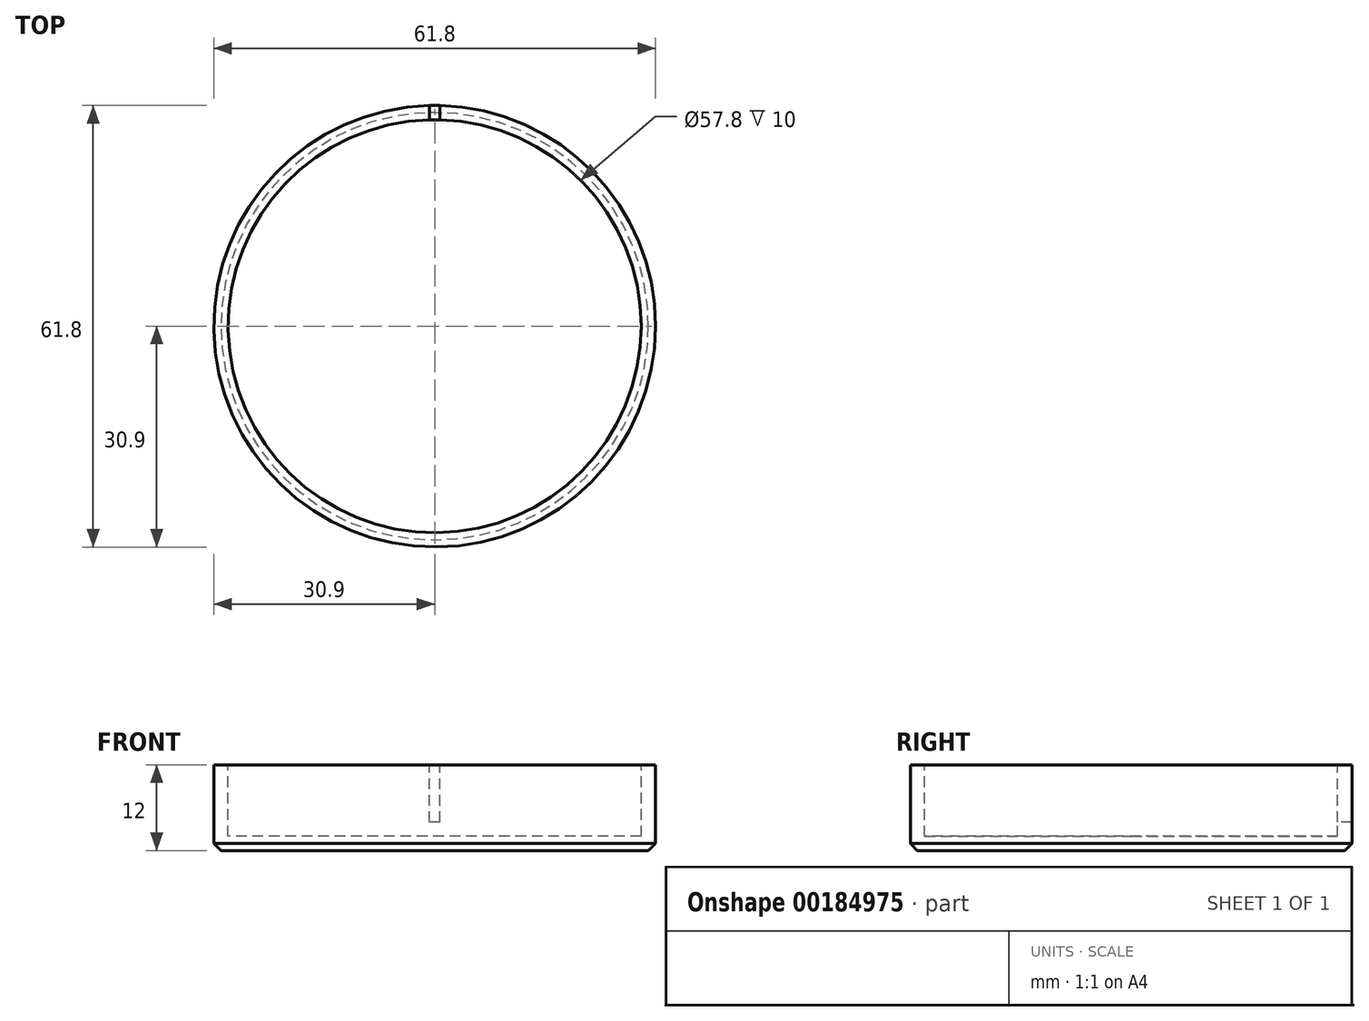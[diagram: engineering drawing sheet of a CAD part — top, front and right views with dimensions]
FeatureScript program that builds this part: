
annotation { "Feature Type Name" : "Feature", "Feature Type Description" : "" }
export const myFeature = defineFeature(function(context is Context, id is Id, definition is map)
    precondition{}
    {
        {
            var Q0;
            Q0=qCreatedBy(makeId("Front.planeOp"),FACE);
            var sketch = newSketch(context, id + "F0", { "sketchPlane" : qUnion([Q0])});
            skLineSegment(sketch, "E0", {"start": v(0, 0) * mm, "end": v(-30.9, 0) * mm});
            skLineSegment(sketch, "E1", {"start": v(-30.9, 0) * mm, "end": v(-30.9, 12) * mm});
            skLineSegment(sketch, "E2", {"start": v(-30.9, 12) * mm, "end": v(-28.9, 12) * mm});
            skLineSegment(sketch, "E3", {"start": v(-28.9, 12) * mm, "end": v(-28.9, 2) * mm});
            skLineSegment(sketch, "E4", {"start": v(-28.9, 2) * mm, "end": v(0, 2) * mm});
            skLineSegment(sketch, "E5", {"start": v(0, 2) * mm, "end": v(0, 0) * mm});
            skSolve(sketch);
        }
        {
            var Q0;
            Q0=makeQuery(id+"F0.imprint","IMPRINT",FACE,{"disambiguationData":[TD([[makeQuery(id+"F0.imprint","IMPRINT",EDGE,{"derivedFrom":sQuery(id+"F0.wireOp",EDGE,"E0")}),-1.0]])]});
            var Q1;
            Q1=sQuery(id+"F0.wireOp",EDGE,"E5");
            revolve(context, id + "F1", {"entities" : qUnion([Q0]), "axis" : qUnion([Q1]), "revolveType" : RevolveType.FULL});
        }
        {
            var Q0;
            Q0=qCreatedBy(makeId("Top.planeOp"),FACE);
            cPlane(context, id + "F2", {"entities" : qUnion([Q0]), "cplaneType" : CPlaneType.OFFSET, "offset" : 12 * mm, "width" : 150 * mm, "height" : 150 * mm});
        }
        {
            var Q0;
            Q0=qCreatedBy(id+"F2.planeOp",FACE);
            var sketch = newSketch(context, id + "F3", { "sketchPlane" : qUnion([Q0])});
            skLineSegment(sketch, "E6.bottom", {"start": v(-0.75, 31.53) * mm, "end": v(0.75, 31.53) * mm});
            skLineSegment(sketch, "E6.top", {"start": v(-0.75, 27.23) * mm, "end": v(0.75, 27.23) * mm});
            skLineSegment(sketch, "E6.left", {"start": v(-0.75, 31.53) * mm, "end": v(-0.75, 27.23) * mm});
            skLineSegment(sketch, "E6.right", {"start": v(0.75, 31.53) * mm, "end": v(0.75, 27.23) * mm});
            skSolve(sketch);
        }
        {
            var Q0;
            Q0=makeQuery(id+"F3.imprint","IMPRINT",FACE,{"disambiguationData":[TD([[makeQuery(id+"F3.imprint","IMPRINT",EDGE,{"derivedFrom":sQuery(id+"F3.wireOp",EDGE,"E6.bottom")}),-1.0]])]});
            extrude(context, id + "F4", {"entities" : qUnion([Q0]), "operationType" : NewBodyOperationType.REMOVE, "oppositeDirection" : true, "depth" : 8 * mm});
        }
        {
            var Q0;
            Q0=makeQuery(id+"F1.opRevolve","SWEPT_EDGE",EDGE,{"disambiguationData":[OSD([sQuery(id+"F0.wireOp",EDGE,"E0"),sQuery(id+"F0.wireOp",EDGE,"E1")])]});
            chamfer(context, id + "F5", {"entities" : qUnion([Q0]), "width" : 1 * mm, "tangentPropagation" : true});
        }
    });
